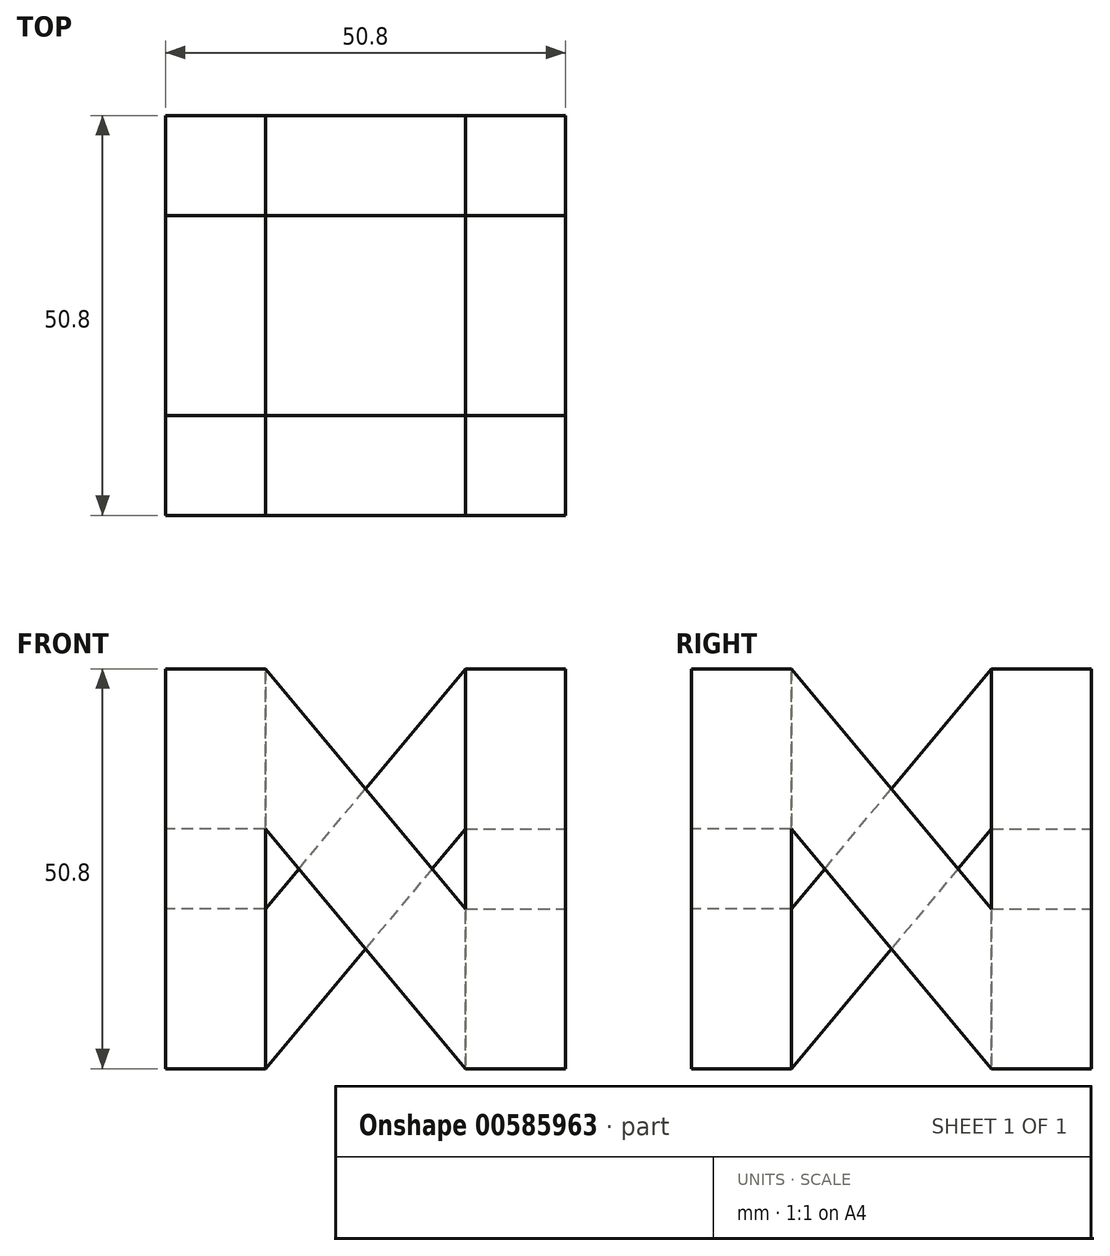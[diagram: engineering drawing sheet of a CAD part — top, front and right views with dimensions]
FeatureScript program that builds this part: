
annotation { "Feature Type Name" : "Feature", "Feature Type Description" : "" }
export const myFeature = defineFeature(function(context is Context, id is Id, definition is map)
    precondition{}
    {
        {
            var Q0;
            Q0=qCreatedBy(makeId("Top.planeOp"),FACE);
            var sketch = newSketch(context, id + "F0", { "sketchPlane" : qUnion([Q0])});
            skLineSegment(sketch, "E0.bottom", {"start": v(0, 0) * mm, "end": v(50.8, 0) * mm});
            skLineSegment(sketch, "E0.top", {"start": v(0, 50.8) * mm, "end": v(50.8, 50.8) * mm});
            skLineSegment(sketch, "E0.left", {"start": v(0, 0) * mm, "end": v(0, 50.8) * mm});
            skLineSegment(sketch, "E0.right", {"start": v(50.8, 0) * mm, "end": v(50.8, 50.8) * mm});
            skLineSegment(sketch, "E1.bottom", {"start": v(12.7, 38.1) * mm, "end": v(38.1, 38.1) * mm});
            skLineSegment(sketch, "E1.top", {"start": v(12.7, 12.7) * mm, "end": v(38.1, 12.7) * mm});
            skLineSegment(sketch, "E1.left", {"start": v(12.7, 38.1) * mm, "end": v(12.7, 12.7) * mm});
            skLineSegment(sketch, "E1.right", {"start": v(38.1, 38.1) * mm, "end": v(38.1, 12.7) * mm});
            skSolve(sketch);
        }
        {
            var Q0;
            Q0 = qSketchRegion(id + "F0", true);
            extrude(context, id + "F1", {"entities" : qUnion([Q0]), "depth" : 50.8 * mm, "offsetDistance" : 25.4 * mm});
        }
        {
            var Q0;
            Q0=makeQuery(id+"F1.opExtrude","SWEPT_FACE",FACE,{"disambiguationData":[OSD([sQuery(id+"F0.wireOp",EDGE,"E0.bottom")])]});
            var sketch = newSketch(context, id + "F2", { "sketchPlane" : qUnion([Q0])});
            skLineSegment(sketch, "E2", {"start": v(12.7, 0) * mm, "end": v(12.7, 30.48) * mm});
            skLineSegment(sketch, "E3", {"start": v(12.7, 30.48) * mm, "end": v(38.1, 0) * mm});
            skLineSegment(sketch, "E4", {"start": v(12.7, 0) * mm, "end": v(38.1, 0) * mm});
            skLineSegment(sketch, "E5", {"start": v(38.1, 50.8) * mm, "end": v(38.1, 20.32) * mm});
            skLineSegment(sketch, "E6", {"start": v(38.1, 20.32) * mm, "end": v(12.7, 50.8) * mm});
            skLineSegment(sketch, "E7", {"start": v(12.7, 50.8) * mm, "end": v(38.1, 50.8) * mm});
            skSolve(sketch);
        }
        {
            var Q0;
            Q0 = qSketchRegion(id + "F2", true);
            extrude(context, id + "F3", {"entities" : qUnion([Q0]), "operationType" : NewBodyOperationType.REMOVE, "oppositeDirection" : true, "depth" : 12.7 * mm, "offsetDistance" : 25.4 * mm});
        }
        {
            var Q0;
            Q0=makeQuery(id+"F1.opExtrude","SWEPT_FACE",FACE,{"disambiguationData":[OSD([sQuery(id+"F0.wireOp",EDGE,"E0.right")])]});
            var sketch = newSketch(context, id + "F4", { "sketchPlane" : qUnion([Q0])});
            skLineSegment(sketch, "E8", {"start": v(12.7, 0) * mm, "end": v(12.7, 30.48) * mm});
            skLineSegment(sketch, "E9", {"start": v(12.7, 30.48) * mm, "end": v(38.1, 0) * mm});
            skLineSegment(sketch, "E10", {"start": v(38.1, 0) * mm, "end": v(12.7, 0) * mm});
            skLineSegment(sketch, "E11", {"start": v(38.1, 50.8) * mm, "end": v(38.1, 20.32) * mm});
            skLineSegment(sketch, "E12", {"start": v(38.1, 20.32) * mm, "end": v(12.7, 50.8) * mm});
            skLineSegment(sketch, "E13", {"start": v(12.7, 50.8) * mm, "end": v(38.1, 50.8) * mm});
            skSolve(sketch);
        }
        {
            var Q0;
            Q0 = qSketchRegion(id + "F4", true);
            extrude(context, id + "F5", {"entities" : qUnion([Q0]), "operationType" : NewBodyOperationType.REMOVE, "oppositeDirection" : true, "depth" : 12.7 * mm, "offsetDistance" : 25.4 * mm});
        }
        {
            var Q0;
            Q0=makeQuery(id+"F1.opExtrude","SWEPT_FACE",FACE,{"disambiguationData":[OSD([sQuery(id+"F0.wireOp",EDGE,"E0.top")])]});
            var sketch = newSketch(context, id + "F6", { "sketchPlane" : qUnion([Q0])});
            skLineSegment(sketch, "E14", {"start": v(-38.1, 0) * mm, "end": v(-38.1, 30.48) * mm});
            skLineSegment(sketch, "E15", {"start": v(-38.1, 30.48) * mm, "end": v(-12.7, 0) * mm});
            skLineSegment(sketch, "E16", {"start": v(-12.7, 0) * mm, "end": v(-38.1, 0) * mm});
            skLineSegment(sketch, "E17", {"start": v(-12.7, 50.8) * mm, "end": v(-12.7, 20.32) * mm});
            skLineSegment(sketch, "E18", {"start": v(-12.7, 20.32) * mm, "end": v(-38.1, 50.8) * mm});
            skLineSegment(sketch, "E19", {"start": v(-38.1, 50.8) * mm, "end": v(-12.7, 50.8) * mm});
            skSolve(sketch);
        }
        {
            var Q0;
            Q0 = qSketchRegion(id + "F6", true);
            extrude(context, id + "F7", {"entities" : qUnion([Q0]), "operationType" : NewBodyOperationType.REMOVE, "oppositeDirection" : true, "depth" : 12.7 * mm, "offsetDistance" : 25.4 * mm});
        }
        {
            var Q0;
            Q0=makeQuery(id+"F1.opExtrude","SWEPT_FACE",FACE,{"disambiguationData":[OSD([sQuery(id+"F0.wireOp",EDGE,"E0.left")])]});
            var sketch = newSketch(context, id + "F8", { "sketchPlane" : qUnion([Q0])});
            skLineSegment(sketch, "E20", {"start": v(-38.1, 0) * mm, "end": v(-38.1, 30.48) * mm});
            skLineSegment(sketch, "E21", {"start": v(-38.1, 30.48) * mm, "end": v(-12.7, 0) * mm});
            skLineSegment(sketch, "E22", {"start": v(-12.7, 0) * mm, "end": v(-38.1, 0) * mm});
            skLineSegment(sketch, "E23", {"start": v(-12.7, 50.8) * mm, "end": v(-12.7, 20.32) * mm});
            skLineSegment(sketch, "E24", {"start": v(-12.7, 20.32) * mm, "end": v(-38.1, 50.8) * mm});
            skLineSegment(sketch, "E25", {"start": v(-38.1, 50.8) * mm, "end": v(-12.7, 50.8) * mm});
            skSolve(sketch);
        }
        {
            var Q0;
            Q0 = qSketchRegion(id + "F8", true);
            extrude(context, id + "F9", {"entities" : qUnion([Q0]), "operationType" : NewBodyOperationType.REMOVE, "oppositeDirection" : true, "depth" : 12.7 * mm, "offsetDistance" : 25.4 * mm});
        }
    });
